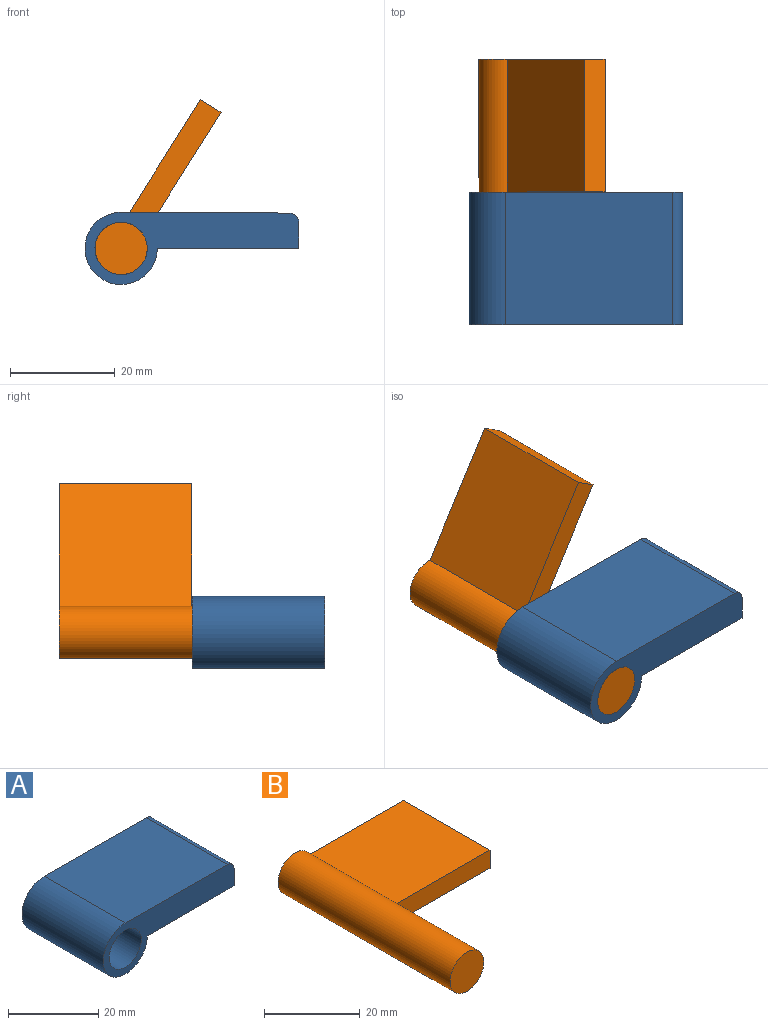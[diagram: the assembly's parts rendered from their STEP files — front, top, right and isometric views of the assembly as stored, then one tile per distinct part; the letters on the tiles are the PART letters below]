
ASSEMBLY  parts=2 mates=1
PART A: 8 faces, bbox 40.9x25.4x13.8 mm
  f0: cylinder r=6.91mm len=25.4mm, axis (0,1,0), area 827.9mm2, adj f1,f4,f6,f7
  f1: plane 27.12x25.4mm, normal (0,0,-1), area 688.8mm2, adj f0,f2,f6,f7
  f2: plane 25.4x4.77mm, normal (1,0,0), area 121.1mm2, adj f1,f3,f6,f7
  f3: cylinder r=2mm len=25.4mm, axis (0,1,0), area 79.6mm2, adj f2,f4,f6,f7
  f4: plane 32.01x25.4mm, normal (0,0,1), area 813mm2, adj f0,f3,f6,f7
  f5: cylinder r=5mm len=25.4mm, axis (0,1,0), area 798mm2, adj f6,f7
  f6: plane 40.94x13.82mm, normal (0,-1,0), area 265.7mm2, adj f0,f1,f2,f3,f4,f5
  f7: plane 40.94x13.82mm, normal (0,1,0), area 265.7mm2, adj f0,f1,f2,f3,f4,f5
PART B: 7 faces, bbox 37.2x50.8x10 mm
  f0: plane 27.78x25.4mm, normal (0,0,1), area 705.5mm2, adj f2,f3,f4,f5
  f1: plane 27.78x25.4mm, normal (0,0,-1), area 705.5mm2, adj f2,f3,f4,f5
  f2: plane 25.4x4.64mm, normal (1,0,0), area 118mm2, adj f0,f1,f3,f4
  f3: plane 27.78x4.64mm, normal (0,-1,0), area 127.2mm2, adj f0,f1,f2,f5
  f4: plane 37.2x10mm, normal (0,1,0), area 205.7mm2, adj f0,f1,f2,f5
  f5: cylinder r=5mm len=50.8mm, axis (0,1,0), area 1473.2mm2, adj f0,f1,f3,f4,f6
  f6: plane 10x10mm, normal (0,-1,0), area 78.5mm2, adj f5
PLACE A t=(2.65,17.85,-0.41)mm fixed
PLACE B rot(axis=(0,-1,0),57.8deg) t=(15.22,43.25,-7.38)mm
MATE revolute B.f5 <-> A.f5  axis (0,-1,0) through (-4.17,-7.55,-0.41)mm
